# Revit family: Keilhauer-GSD-Table-Counter_Height-Rounded_Rectangle-
name_source: partatom
category: Furniture
revit_build: Autodesk Revit 2016 (Build: 20150220_1215(x64)
units: mm (PartAtom-declared; Revit-internal decimal feet)

## family parameters
Always vertical = Yes
Cut with Voids When Loaded = No
OmniClass Number = 23.40.20.00
OmniClass Title = General Furniture and Specialties
Room Calculation Point = No
Shared = No
Work Plane-Based = No

## types (6) — shared parameters
Assembly Code = E2020200
Height = 36"
Keynote = 12500
Leg Dist = 10"
Low Emitting Finish = Yes
Low Emitting Material = Yes
Manufacturer = Keilhauer
Product Documentation Link = https://keilhauer.com
Revit File Built By = https://servex-us.com
Salvage or Reuse = Yes
Type Comments = GSD
URL = https://keilhauer.com
zero-valued in all types: Percentage of Recycled Content

## per-type parameters (varying)
| type | 10236 | 10242 | 7136 | 7142 | 8636 | 8642 | Depth | Description | Width |
| 89510 | No | No | Yes | No | No | No | 36" | Rounded rectangle 36" x 71", counter height | 71" |
| 89511 | No | No | No | No | Yes | No | 36" | Rounded rectangle 36" x 86", counter height | 86" |
| 89512 | Yes | No | No | No | No | No | 36" | Rounded rectangle 36" x 102", counter height | 102" |
| 89513 | No | No | No | Yes | No | No | 42" | Rounded rectangle 42" x 71", counter height | 71" |
| 89514 | No | No | No | No | No | Yes | 42" | Rounded rectangle 42" x 86", counter height | 86" |
| 89515 | No | Yes | No | No | No | No | 42" | Rounded rectangle 42" x 102", counter height | 102" |

note: column(s) folded — value = type name in every type: Model

## geometry (parser evidence)
native form markers: Sweep x8
no freeform markers — native parametric forms only
